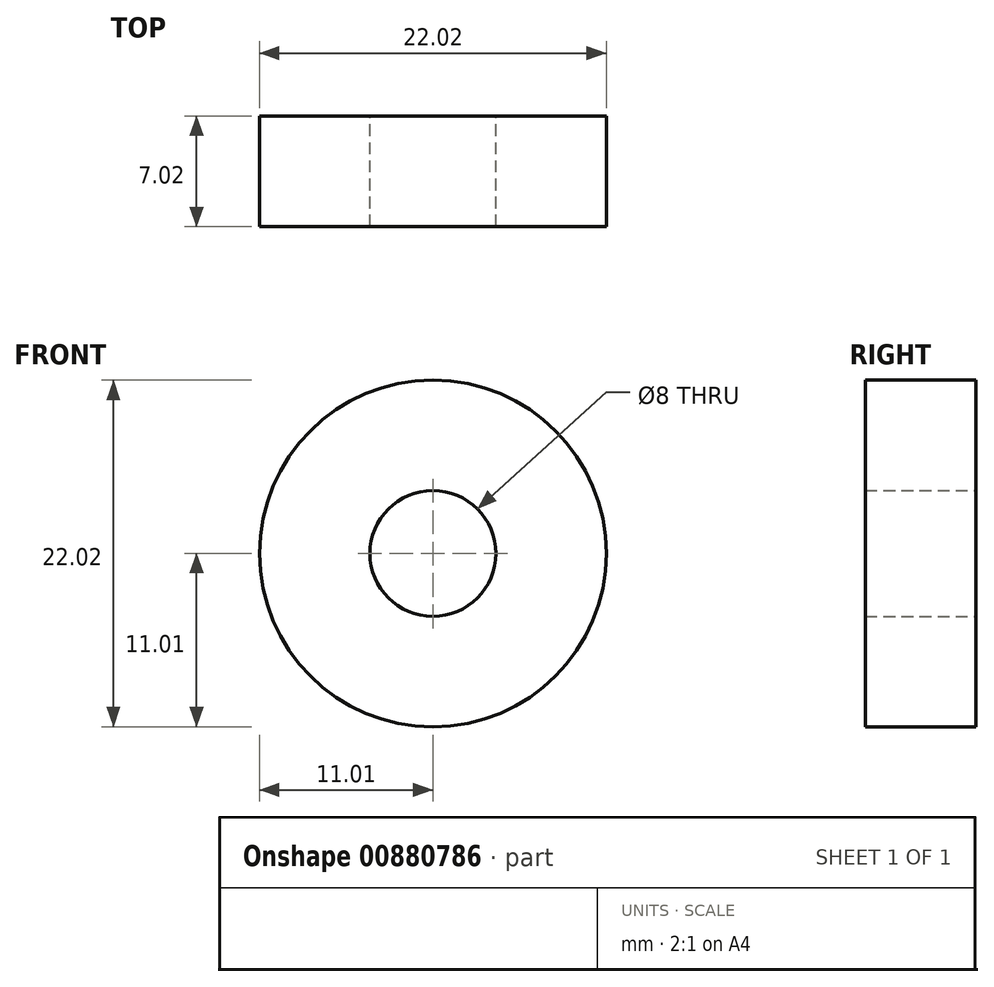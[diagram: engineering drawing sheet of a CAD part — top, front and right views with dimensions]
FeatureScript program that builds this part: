
annotation { "Feature Type Name" : "Feature", "Feature Type Description" : "" }
export const myFeature = defineFeature(function(context is Context, id is Id, definition is map)
    precondition{}
    {
        {
            var Q0;
            Q0=qCreatedBy(makeId("Front.planeOp"),FACE);
            var sketch = newSketch(context, id + "F0", { "sketchPlane" : qUnion([Q0])});
            skCircle(sketch, "E0", {"center": v(0, 0) * mm, "radius": 11.01 * mm});
            skCircle(sketch, "E1", {"center": v(0, 0) * mm, "radius": 4 * mm});
            skSolve(sketch);
        }
        {
            var Q0;
            Q0=makeQuery(id+"F0.imprint","IMPRINT",FACE,{"disambiguationData":[TD([[makeQuery(id+"F0.imprint","IMPRINT",EDGE,{"derivedFrom":sQuery(id+"F0.wireOp",EDGE,"E0")}),1.0]])]});
            extrude(context, id + "F1", {"entities" : qUnion([Q0]), "depth" : 7 * mm, "offsetDistance" : 25.4 * mm, "symmetric" : true});
        }
    });
